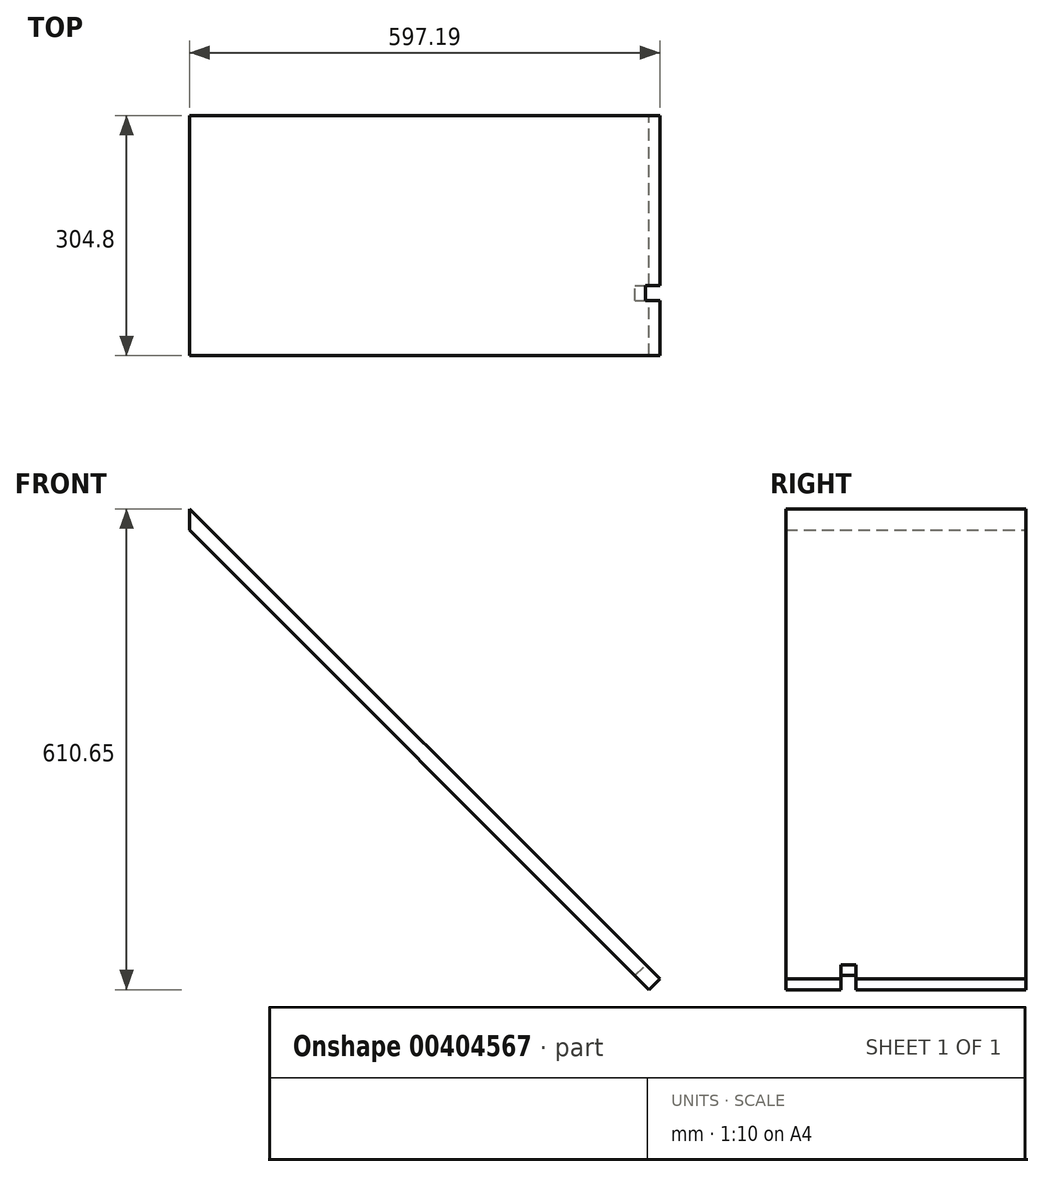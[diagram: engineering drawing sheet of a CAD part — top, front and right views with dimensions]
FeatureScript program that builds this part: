
annotation { "Feature Type Name" : "Feature", "Feature Type Description" : "" }
export const myFeature = defineFeature(function(context is Context, id is Id, definition is map)
    precondition{}
    {
        {
            var Q0;
            Q0=qCreatedBy(makeId("Front.planeOp"),FACE);
            var sketch = newSketch(context, id + "F0", { "sketchPlane" : qUnion([Q0])});
            skLineSegment(sketch, "E0.right", {"start": v(-341.41, 790.1) * mm, "end": v(-341.41, 817.04) * mm});
            skLineSegment(sketch, "E1.MirrorCS", {"start": v(242.3, 206.39) * mm, "end": v(-341.41, 790.1) * mm});
            skLineSegment(sketch, "E2.MirrorCS", {"start": v(255.78, 219.86) * mm, "end": v(-341.41, 817.04) * mm});
            skLineSegment(sketch, "E3", {"start": v(255.78, 219.86) * mm, "end": v(242.3, 206.39) * mm});
            skSolve(sketch);
        }
        {
            var Q0;
            Q0=qSketchRegion(id+"F0",true);
            extrude(context, id + "F1", {"entities" : qUnion([Q0]), "endBound" : BoundingType.SYMMETRIC, "depth" : 304.8 * mm});
        }
        {
            var Q0;
            Q0=makeQuery(id+"F1.opExtrude","SWEPT_FACE",FACE,{"disambiguationData":[OSD([sQuery(id+"F0.wireOp",EDGE,"E2.MirrorCS")])]});
            var sketch = newSketch(context, id + "F2", { "sketchPlane" : qUnion([Q0])});
            skLineSegment(sketch, "E4.bottom", {"start": v(-730.25, -152.4) * mm, "end": v(-711.2, -152.4) * mm});
            skLineSegment(sketch, "E4.top", {"start": v(-730.25, 0) * mm, "end": v(-711.2, 0) * mm});
            skLineSegment(sketch, "E4.left", {"start": v(-730.25, 0) * mm, "end": v(-730.25, -152.4) * mm});
            skLineSegment(sketch, "E4.right", {"start": v(-711.2, 0) * mm, "end": v(-711.2, -152.4) * mm});
            skLineSegment(sketch, "E5.bottom", {"start": v(-622.3, -152.4) * mm, "end": v(-603.25, -152.4) * mm});
            skLineSegment(sketch, "E5.top", {"start": v(-622.3, 0) * mm, "end": v(-603.25, 0) * mm});
            skLineSegment(sketch, "E5.left", {"start": v(-622.3, 0) * mm, "end": v(-622.3, -152.4) * mm});
            skLineSegment(sketch, "E5.right", {"start": v(-603.25, 0) * mm, "end": v(-603.25, -152.4) * mm});
            skLineSegment(sketch, "E6.bottom", {"start": v(-514.35, -152.4) * mm, "end": v(-495.3, -152.4) * mm});
            skLineSegment(sketch, "E6.top", {"start": v(-514.35, 0) * mm, "end": v(-495.3, 0) * mm});
            skLineSegment(sketch, "E6.left", {"start": v(-514.35, 0) * mm, "end": v(-514.35, -152.4) * mm});
            skLineSegment(sketch, "E6.right", {"start": v(-495.3, 0) * mm, "end": v(-495.3, -152.4) * mm});
            skLineSegment(sketch, "E7.bottom", {"start": v(-406.4, -152.4) * mm, "end": v(-387.35, -152.4) * mm});
            skLineSegment(sketch, "E7.top", {"start": v(-406.4, 0) * mm, "end": v(-387.35, 0) * mm});
            skLineSegment(sketch, "E7.left", {"start": v(-406.4, 0) * mm, "end": v(-406.4, -152.4) * mm});
            skLineSegment(sketch, "E7.right", {"start": v(-387.35, 0) * mm, "end": v(-387.35, -152.4) * mm});
            skLineSegment(sketch, "E8.bottom", {"start": v(-298.45, -152.4) * mm, "end": v(-279.4, -152.4) * mm});
            skLineSegment(sketch, "E8.top", {"start": v(-298.45, 0) * mm, "end": v(-279.4, 0) * mm});
            skLineSegment(sketch, "E8.left", {"start": v(-298.45, 0) * mm, "end": v(-298.45, -152.4) * mm});
            skLineSegment(sketch, "E8.right", {"start": v(-279.4, 0) * mm, "end": v(-279.4, -152.4) * mm});
            skLineSegment(sketch, "E9.bottom", {"start": v(-190.5, -152.4) * mm, "end": v(-171.45, -152.4) * mm});
            skLineSegment(sketch, "E9.top", {"start": v(-190.5, 0) * mm, "end": v(-171.45, 0) * mm});
            skLineSegment(sketch, "E9.left", {"start": v(-190.5, 0) * mm, "end": v(-190.5, -152.4) * mm});
            skLineSegment(sketch, "E9.right", {"start": v(-171.45, 0) * mm, "end": v(-171.45, -152.4) * mm});
            skLineSegment(sketch, "E10.bottom", {"start": v(-82.55, -152.4) * mm, "end": v(-63.5, -152.4) * mm});
            skLineSegment(sketch, "E10.top", {"start": v(-82.55, 0) * mm, "end": v(-63.5, 0) * mm});
            skLineSegment(sketch, "E10.left", {"start": v(-82.55, 0) * mm, "end": v(-82.55, -152.4) * mm});
            skLineSegment(sketch, "E10.right", {"start": v(-63.5, 0) * mm, "end": v(-63.5, -152.4) * mm});
            skSolve(sketch);
        }
        {
            var Q0;
            Q0=qSketchRegion(id+"F2",true);
            extrude(context, id + "F3", {"entities" : qUnion([Q0]), "operationType" : NewBodyOperationType.REMOVE, "oppositeDirection" : true, "depth" : 19.05 * mm});
        }
    });
